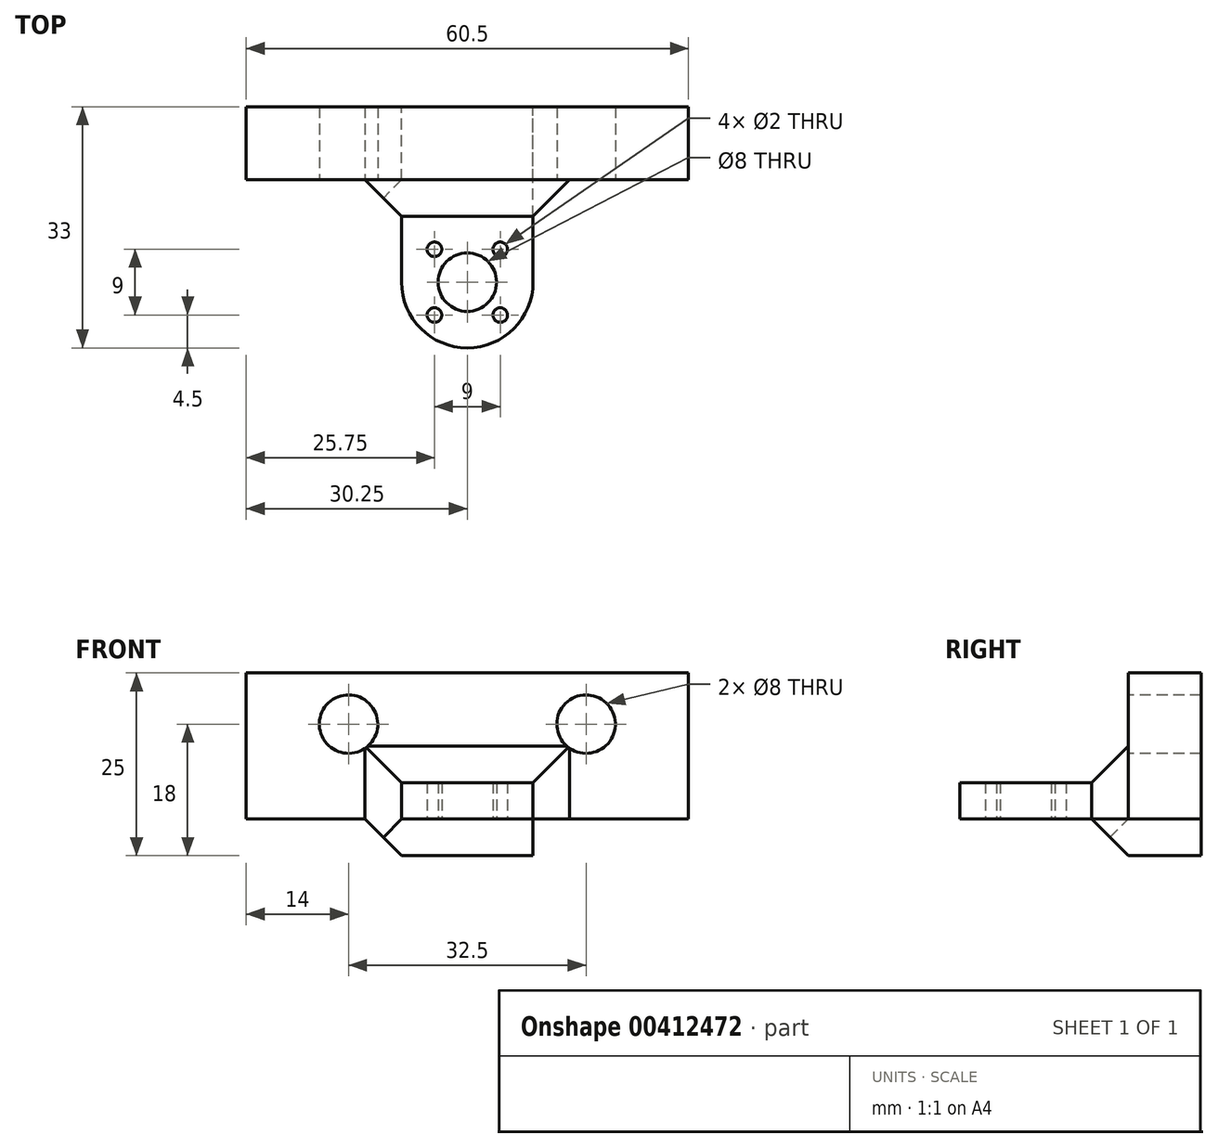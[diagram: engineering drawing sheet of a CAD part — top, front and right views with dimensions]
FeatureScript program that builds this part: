
annotation { "Feature Type Name" : "Feature", "Feature Type Description" : "" }
export const myFeature = defineFeature(function(context is Context, id is Id, definition is map)
    precondition{}
    {
        {
            var Q0;
            Q0=qCreatedBy(makeId("Top.planeOp"),FACE);
            var sketch = newSketch(context, id + "F0", { "sketchPlane" : qUnion([Q0])});
            skCircle(sketch, "E0", {"center": v(0, 0) * mm, "radius": 4 * mm});
            skCircle(sketch, "E1.0", {"center": v(0, 0) * mm, "radius": 9 * mm});
            skLineSegment(sketch, "E2.right", {"start": v(-4.5, 4.5) * mm, "end": v(-4.5, 3.5) * mm});
            skCircle(sketch, "E3", {"center": v(-4.5, 4.5) * mm, "radius": 1 * mm});
            skCircle(sketch, "E4", {"center": v(4.5, 4.5) * mm, "radius": 1 * mm});
            skCircle(sketch, "E5", {"center": v(4.5, -4.5) * mm, "radius": 1 * mm});
            skCircle(sketch, "E6", {"center": v(-4.5, -4.5) * mm, "radius": 1 * mm});
            skLineSegment(sketch, "E7.bottom", {"start": v(-9, 0) * mm, "end": v(9, 0) * mm});
            skLineSegment(sketch, "E7.top", {"start": v(-9, 14) * mm, "end": v(9, 14) * mm});
            skLineSegment(sketch, "E7.left", {"start": v(-9, 0) * mm, "end": v(-9, 14) * mm});
            skLineSegment(sketch, "E7.right", {"start": v(9, 0) * mm, "end": v(9, 14) * mm});
            skLineSegment(sketch, "E8.top", {"start": v(-9, 24) * mm, "end": v(9, 24) * mm});
            skLineSegment(sketch, "E8.left", {"start": v(-9, 14) * mm, "end": v(-9, 24) * mm});
            skLineSegment(sketch, "E8.right", {"start": v(9, 14) * mm, "end": v(9, 24) * mm});
            skCircle(sketch, "E9", {"center": v(20.25, 19) * mm, "radius": 4 * mm});
            skCircle(sketch, "E10", {"center": v(-20.25, 19) * mm, "radius": 4 * mm});
            skLineSegment(sketch, "E11.bottom", {"start": v(-9, 14) * mm, "end": v(-30.25, 14) * mm});
            skLineSegment(sketch, "E11.top", {"start": v(-9, 24) * mm, "end": v(-30.25, 24) * mm});
            skLineSegment(sketch, "E11.right", {"start": v(-30.25, 14) * mm, "end": v(-30.25, 24) * mm});
            skLineSegment(sketch, "E12.bottom", {"start": v(9, 14) * mm, "end": v(30.25, 14) * mm});
            skLineSegment(sketch, "E12.top", {"start": v(9, 24) * mm, "end": v(30.25, 24) * mm});
            skLineSegment(sketch, "E12.right", {"start": v(30.25, 14) * mm, "end": v(30.25, 24) * mm});
            skSolve(sketch);
        }
        {
            var Q0;
            Q0=makeQuery(id+"F0.imprint","IMPRINT",FACE,{"disambiguationData":[TD([[makeQuery(id+"F0.imprint","IMPRINT",EDGE,{"derivedFrom":sQuery(id+"F0.wireOp",EDGE,"E5")}),-1.0]])]});
            var Q1;
            Q1=makeQuery(id+"F0.imprint","IMPRINT",FACE,{"disambiguationData":[TD([[makeQuery(id+"F0.imprint","IMPRINT",EDGE,{"derivedFrom":sQuery(id+"F0.wireOp",EDGE,"E3")}),-1.0]])]});
            var Q2;
            {var subQ0=sQuery(id+"F0.wireOp",EDGE,"E7.left");Q2=makeQuery(id+"F0.imprint","IMPRINT",FACE,{"disambiguationData":[TD([[makeQuery(id+"F0.imprint","IMPRINT",EDGE,{"derivedFrom":subQ0}),-1.0]])]});}
            var Q3;
            Q3=makeQuery(id+"F0.imprint","IMPRINT",FACE,{"disambiguationData":[TD([[makeQuery(id+"F0.imprint","IMPRINT",EDGE,{"derivedFrom":sQuery(id+"F0.wireOp",EDGE,"E7.top")}),1.0]])]});
            extrude(context, id + "F1", {"entities" : qUnion([Q0, Q1, Q2, Q3]), "depth" : 5 * mm});
        }
        {
            var Q0;
            Q0=makeQuery(id+"F0.imprint","IMPRINT",FACE,{"disambiguationData":[TD([[makeQuery(id+"F0.imprint","IMPRINT",EDGE,{"derivedFrom":sQuery(id+"F0.wireOp",EDGE,"E7.top")}),1.0]])]});
            var Q1;
            Q1=makeQuery(id+"F0.imprint","IMPRINT",FACE,{"disambiguationData":[TD([[makeQuery(id+"F0.imprint","IMPRINT",EDGE,{"derivedFrom":sQuery(id+"F0.wireOp",EDGE,"E10")}),-1.0]])]});
            var Q2;
            Q2=makeQuery(id+"F0.imprint","IMPRINT",FACE,{"disambiguationData":[TD([[makeQuery(id+"F0.imprint","IMPRINT",EDGE,{"derivedFrom":sQuery(id+"F0.wireOp",EDGE,"E9")}),-1.0]])]});
            var Q3;
            Q3=makeQuery(id+"F0.imprint","IMPRINT",FACE,{"disambiguationData":[TD([[makeQuery(id+"F0.imprint","IMPRINT",EDGE,{"derivedFrom":sQuery(id+"F0.wireOp",EDGE,"E9")}),1.0]])]});
            var Q4;
            Q4=makeQuery(id+"F0.imprint","IMPRINT",FACE,{"disambiguationData":[TD([[makeQuery(id+"F0.imprint","IMPRINT",EDGE,{"derivedFrom":sQuery(id+"F0.wireOp",EDGE,"E10")}),1.0]])]});
            extrude(context, id + "F2", {"entities" : qUnion([Q0, Q1, Q2, Q3, Q4]), "operationType" : NewBodyOperationType.ADD, "depth" : 20 * mm});
        }
        {
            var Q0;
            Q0=qCreatedBy(makeId("Front.planeOp"),FACE);
            var sketch = newSketch(context, id + "F3", { "sketchPlane" : qUnion([Q0])});
            skLineSegment(sketch, "E13.bottom", {"start": v(30.25, 0) * mm, "end": v(-30.25, 0) * mm});
            skLineSegment(sketch, "E13.top", {"start": v(30.25, 20) * mm, "end": v(-30.25, 20) * mm});
            skLineSegment(sketch, "E13.left", {"start": v(30.25, 0) * mm, "end": v(30.25, 20) * mm});
            skLineSegment(sketch, "E13.right", {"start": v(-30.25, 0) * mm, "end": v(-30.25, 20) * mm});
            skCircle(sketch, "E14", {"center": v(-16.25, 13) * mm, "radius": 4 * mm});
            skCircle(sketch, "E15", {"center": v(16.25, 13) * mm, "radius": 4 * mm});
            skSolve(sketch);
        }
        {
            var Q0;
            Q0=makeQuery(id+"F3.imprint","IMPRINT",FACE,{"disambiguationData":[TD([[makeQuery(id+"F3.imprint","IMPRINT",EDGE,{"derivedFrom":sQuery(id+"F3.wireOp",EDGE,"E14")}),1.0]])]});
            var Q1;
            Q1=makeQuery(id+"F3.imprint","IMPRINT",FACE,{"disambiguationData":[TD([[makeQuery(id+"F3.imprint","IMPRINT",EDGE,{"derivedFrom":sQuery(id+"F3.wireOp",EDGE,"E15")}),1.0]])]});
            extrude(context, id + "F4", {"entities" : qUnion([Q0, Q1]), "operationType" : NewBodyOperationType.REMOVE, "oppositeDirection" : true, "depth" : 25 * mm});
        }
        {
            var Q0;
            Q0=makeQuery(id+"F0.imprint","IMPRINT",FACE,{"disambiguationData":[TD([[makeQuery(id+"F0.imprint","IMPRINT",EDGE,{"derivedFrom":sQuery(id+"F0.wireOp",EDGE,"E8.top")}),1.0]])]});
            var Q1;
            Q1=makeQuery(id+"F0.imprint","IMPRINT",FACE,{"disambiguationData":[TD([[makeQuery(id+"F0.imprint","IMPRINT",EDGE,{"derivedFrom":sQuery(id+"F0.wireOp",EDGE,"E7.top")}),1.0]])]});
            extrude(context, id + "F5", {"entities" : qUnion([Q0, Q1]), "operationType" : NewBodyOperationType.ADD, "oppositeDirection" : true, "depth" : 5 * mm});
        }
        {
            var Q0;
            Q0=makeQuery(id+"F5.opExtrude","CAP_EDGE",EDGE,{"disambiguationData":[OSD([sQuery(id+"F0.wireOp",EDGE,"E7.top")])],"isStart":true});
            chamfer(context, id + "F6", {"entities" : qUnion([Q0]), "width" : 5 * mm, "tangentPropagation" : true});
        }
        {
            var Q0;
            Q0=makeQuery(id+"F2.boolean.opBoolean","INTERSECT",EDGE,{"derivedFrom":[makeQuery(id+"F1.opExtrude","SWEPT_FACE",FACE,{"disambiguationData":[OSD([sQuery(id+"F0.wireOp",EDGE,"E7.left"),sQuery(id+"F0.wireOp",EDGE,"E8.left")])]}),makeQuery(id+"F2.opExtrude","SWEPT_FACE",FACE,{"disambiguationData":[OSD([sQuery(id+"F0.wireOp",EDGE,"E7.top"),sQuery(id+"F0.wireOp",EDGE,"E11.bottom"),sQuery(id+"F0.wireOp",EDGE,"E12.bottom")])]})]});
            var Q1;
            Q1=makeQuery(id+"F2.boolean.opBoolean","INTERSECT",EDGE,{"derivedFrom":[makeQuery(id+"F1.opExtrude","CAP_FACE",FACE,{"disambiguationData":[OSD([sQuery(id+"F0.wireOp",EDGE,"E0"),sQuery(id+"F0.wireOp",EDGE,"E1.0"),sQuery(id+"F0.wireOp",EDGE,"E3"),sQuery(id+"F0.wireOp",EDGE,"E4"),sQuery(id+"F0.wireOp",EDGE,"E5"),sQuery(id+"F0.wireOp",EDGE,"E6"),sQuery(id+"F0.wireOp",EDGE,"E7.left"),sQuery(id+"F0.wireOp",EDGE,"E7.right"),sQuery(id+"F0.wireOp",EDGE,"E8.top"),sQuery(id+"F0.wireOp",EDGE,"E8.left"),sQuery(id+"F0.wireOp",EDGE,"E8.right")])],"isStart":false}),makeQuery(id+"F2.opExtrude","SWEPT_FACE",FACE,{"disambiguationData":[OSD([sQuery(id+"F0.wireOp",EDGE,"E7.top"),sQuery(id+"F0.wireOp",EDGE,"E11.bottom"),sQuery(id+"F0.wireOp",EDGE,"E12.bottom")])]})]});
            var Q2;
            Q2=makeQuery(id+"F2.boolean.opBoolean","INTERSECT",EDGE,{"derivedFrom":[makeQuery(id+"F1.opExtrude","SWEPT_FACE",FACE,{"disambiguationData":[OSD([sQuery(id+"F0.wireOp",EDGE,"E7.right"),sQuery(id+"F0.wireOp",EDGE,"E8.right")])]}),makeQuery(id+"F2.opExtrude","SWEPT_FACE",FACE,{"disambiguationData":[OSD([sQuery(id+"F0.wireOp",EDGE,"E7.top"),sQuery(id+"F0.wireOp",EDGE,"E11.bottom"),sQuery(id+"F0.wireOp",EDGE,"E12.bottom")])]})]});
            var Q3;
            {var subQ0=sQuery(id+"F0.wireOp",EDGE,"E8.right");var subQ1=sQuery(id+"F0.wireOp",EDGE,"E8.top");var subQ2=sQuery(id+"F0.wireOp",EDGE,"h5OpQ96g-VMLb-Uhrf-ynHz-C4l4hl0HPRqp.right");Q3=makeQuery(id+"F5.boolean.opBoolean","SPLIT",EDGE,{"disambiguationData":[topologyDisambiguationEdgeConnected([makeQuery(id+"F2.opExtrude","CAP_FACE",FACE,{"disambiguationData":[OSD([sQuery(id+"F0.wireOp",EDGE,"E7.top"),subQ1,sQuery(id+"F0.wireOp",EDGE,"E11.bottom"),sQuery(id+"F0.wireOp",EDGE,"E11.top"),sQuery(id+"F0.wireOp",EDGE,"E11.right"),sQuery(id+"F0.wireOp",EDGE,"E12.bottom"),sQuery(id+"F0.wireOp",EDGE,"E12.top"),sQuery(id+"F0.wireOp",EDGE,"E12.right")])],"isStart":true})])],"derivedFrom":makeQuery(id+"F5.opExtrude","CAP_EDGE",EDGE,{"disambiguationData":[OSD([subQ2,subQ0])],"isStart":true})});}
            var Q4;
            {var subQ0=sQuery(id+"F0.wireOp",EDGE,"E8.left");var subQ1=sQuery(id+"F0.wireOp",EDGE,"E8.top");var subQ2=sQuery(id+"F0.wireOp",EDGE,"h5OpQ96g-VMLb-Uhrf-ynHz-C4l4hl0HPRqp.left");Q4=makeQuery(id+"F5.boolean.opBoolean","SPLIT",EDGE,{"disambiguationData":[topologyDisambiguationEdgeConnected([makeQuery(id+"F2.opExtrude","CAP_FACE",FACE,{"disambiguationData":[OSD([sQuery(id+"F0.wireOp",EDGE,"E7.top"),subQ1,sQuery(id+"F0.wireOp",EDGE,"E11.bottom"),sQuery(id+"F0.wireOp",EDGE,"E11.top"),sQuery(id+"F0.wireOp",EDGE,"E11.right"),sQuery(id+"F0.wireOp",EDGE,"E12.bottom"),sQuery(id+"F0.wireOp",EDGE,"E12.top"),sQuery(id+"F0.wireOp",EDGE,"E12.right")])],"isStart":true})])],"derivedFrom":makeQuery(id+"F5.opExtrude","CAP_EDGE",EDGE,{"disambiguationData":[OSD([subQ2,subQ0])],"isStart":true})});}
            chamfer(context, id + "F7", {"entities" : qUnion([Q0, Q1, Q2, Q3, Q4]), "width" : 5 * mm, "tangentPropagation" : true});
        }
    });
